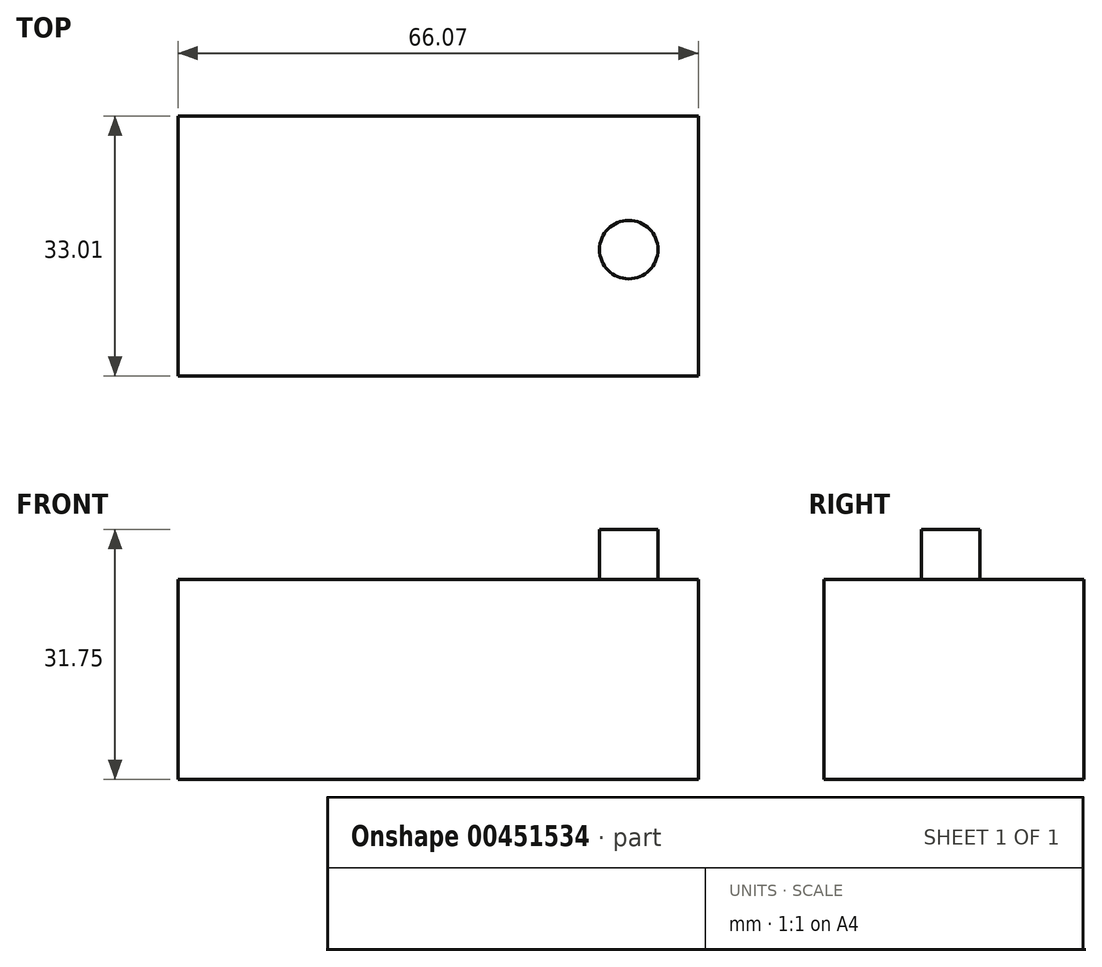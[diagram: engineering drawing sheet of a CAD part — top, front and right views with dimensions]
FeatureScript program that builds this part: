
annotation { "Feature Type Name" : "Feature", "Feature Type Description" : "" }
export const myFeature = defineFeature(function(context is Context, id is Id, definition is map)
    precondition{}
    {
        {
            var Q0;
            Q0=qCreatedBy(makeId("Top.planeOp"),FACE);
            var sketch = newSketch(context, id + "F0", { "sketchPlane" : qUnion([Q0])});
            skLineSegment(sketch, "E0.bottom", {"start": v(-66.07, -57.62) * mm, "end": v(0, -57.62) * mm});
            skLineSegment(sketch, "E0.top", {"start": v(-66.07, -24.6) * mm, "end": v(0, -24.6) * mm});
            skLineSegment(sketch, "E0.left", {"start": v(-66.07, -57.62) * mm, "end": v(-66.07, -24.6) * mm});
            skLineSegment(sketch, "E0.right", {"start": v(0, -57.62) * mm, "end": v(0, -24.6) * mm});
            skSolve(sketch);
        }
        {
            var Q0;
            Q0=makeQuery(id+"F0.imprint","IMPRINT",FACE,{"disambiguationData":[TD([[makeQuery(id+"F0.imprint","IMPRINT",EDGE,{"derivedFrom":sQuery(id+"F0.wireOp",EDGE,"E0.bottom")}),1.0]])]});
            extrude(context, id + "F1", {"entities" : qUnion([Q0]), "endBound" : BoundingType.SYMMETRIC, "depth" : 25.4 * mm});
        }
        {
            var Q0;
            Q0=makeQuery(id+"F1.opExtrude","CAP_FACE",FACE,{"disambiguationData":[OSD([sQuery(id+"F0.wireOp",EDGE,"E0.bottom"),sQuery(id+"F0.wireOp",EDGE,"E0.top"),sQuery(id+"F0.wireOp",EDGE,"E0.left"),sQuery(id+"F0.wireOp",EDGE,"E0.right")])],"isStart":false});
            var sketch = newSketch(context, id + "F2", { "sketchPlane" : qUnion([Q0])});
            skCircle(sketch, "E1", {"center": v(-8.83, -41.57) * mm, "radius": 3.71 * mm});
            skSolve(sketch);
        }
        {
            var Q0;
            Q0=makeQuery(id+"F2.imprint","IMPRINT",FACE,{"disambiguationData":[TD([[makeQuery(id+"F2.imprint","IMPRINT",EDGE,{"derivedFrom":sQuery(id+"F2.wireOp",EDGE,"E1")}),1.0]])]});
            extrude(context, id + "F3", {"entities" : qUnion([Q0]), "operationType" : NewBodyOperationType.ADD, "depth" : 6.35 * mm});
        }
    });
